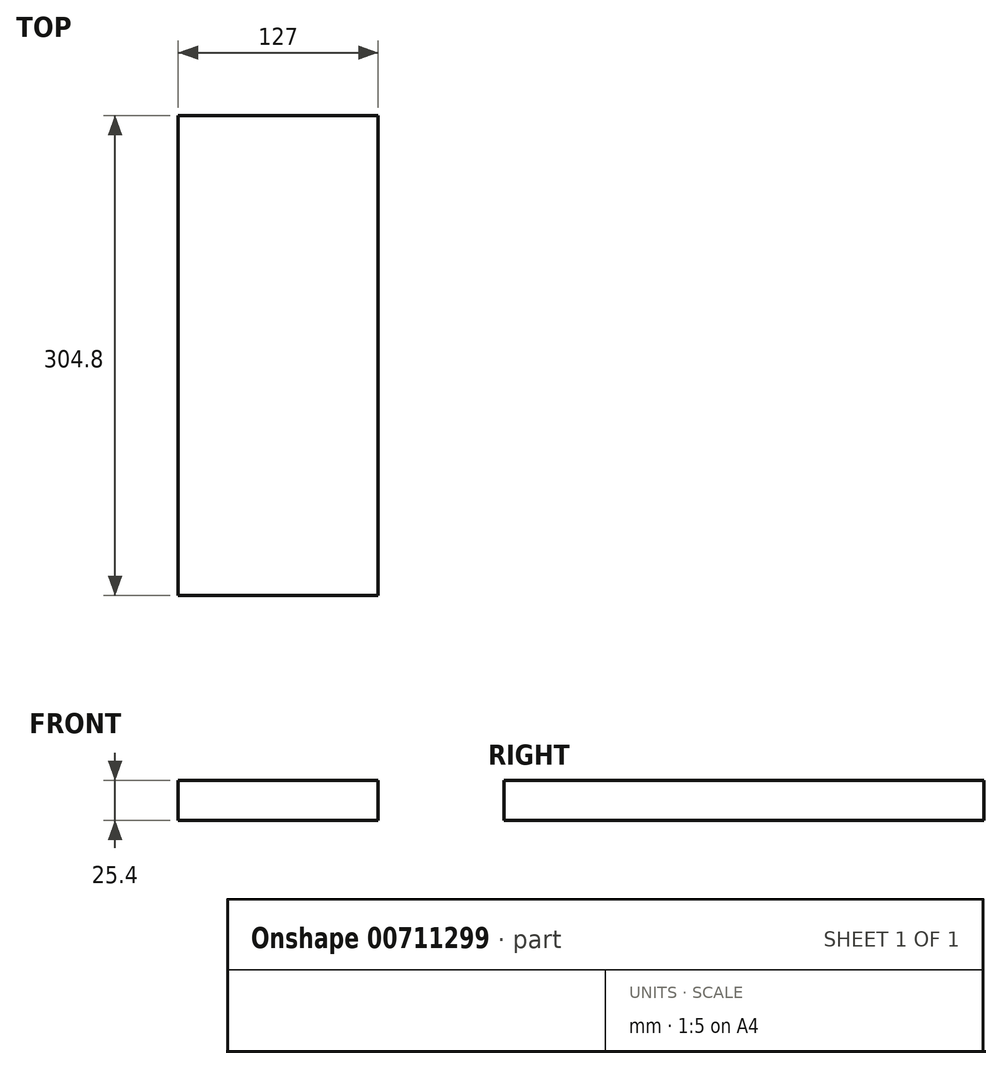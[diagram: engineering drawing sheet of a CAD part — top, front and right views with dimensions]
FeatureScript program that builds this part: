
annotation { "Feature Type Name" : "Feature", "Feature Type Description" : "" }
export const myFeature = defineFeature(function(context is Context, id is Id, definition is map)
    precondition{}
    {
        {
            var Q0;
            Q0=qCreatedBy(makeId("Top.planeOp"),FACE);
            var sketch = newSketch(context, id + "F0", { "sketchPlane" : qUnion([Q0])});
            skLineSegment(sketch, "E0.bottom", {"start": v(-63.35, 192.57) * mm, "end": v(63.65, 192.57) * mm});
            skLineSegment(sketch, "E0.top", {"start": v(-63.35, -112.23) * mm, "end": v(63.65, -112.23) * mm});
            skLineSegment(sketch, "E0.left", {"start": v(-63.35, 192.57) * mm, "end": v(-63.35, -112.23) * mm});
            skLineSegment(sketch, "E0.right", {"start": v(63.65, 192.57) * mm, "end": v(63.65, -112.23) * mm});
            skSolve(sketch);
        }
        {
            var Q0;
            Q0 = qSketchRegion(id + "F0", true);
            extrude(context, id + "F1", {"entities" : qUnion([Q0]), "endBound" : BoundingType.SYMMETRIC, "depth" : 25.4 * mm, "offsetDistance" : 25.4 * mm});
        }
    });
